# Revit family: Ladder_Ships_ALACO_Mezzanine-M60-80
name_source: partatom
category: Generic Models
units: mm (PartAtom-declared; Revit-internal decimal feet)

## family parameters
Can host rebar = No
Classification Number = 23.30.70.17.17
Cut with Voids When Loaded = No
Host = Face
Maintain Annotation Orientation = No
Part Type = Normal
Room Calculation Point = No
Round Connector Dimension = Use Diameter
Shared = No

## types (8) — shared parameters
Assembly Code = B1010700
Capacity = 1500 lbs per Rung
Default Elevation = 0' - 0"
Keynote = 05515
Manufacturer = ALACO Ladder Co
Manufacturer Fax = 909-591-7565
Manufacturer Website = http://alacoladder.com
Product Data = http://www.arcat.com
Revision = R1_2016-12
Standards Conformance = OSHA 1910.27
URL = http://alacoladder.com
Unit Width = 2' - 0"
handrailradius = 0' - 5 7/8"
zero-valued in all types: Expected Lifespan (Years), Maintenance Schedule (Months), Warranty Duration (Years)

## per-type parameters (varying)
| type | Description | Handrail Offset | Ladder Incline | Max Height | Model | Rail Depth | Step Height | Step Width | Top Step Offset from Surface | Use Extended Handrails | Use Flush Handrails |
| 80 Degree Incline Flush Handrail | ALACO Mezzanine Access Incline Ships Ladder - M80 as Specified | 0' - 7" | 80.00° | 14' - 0" | M80xxx | 0' - 2 13/16" | 0' - 11 13/16" | 0' - 3" | 0' - 2 1/4" | No | Yes |
| 75 Degree Incline Flush Handrail | ALACO Mezzanine Access Incline Ships Ladder - M75 as Specified | 0' - 7" | 75.00° | 17' - 0" | M75xxx | 0' - 4 1/8" | 0' - 11 5/8" | 0' - 4 1/4" | 0' - 1" | No | Yes |
| 70 Degree Incline Flush Handrail | ALACO Mezzanine Access Incline Ships Ladder - M70 as Specified | 0' - 7" | 70.00° | 17' - 0" | M70xxx | 0' - 4 1/8" | 0' - 11 1/4" | 0' - 4" | 0' - 0 7/8" | No | Yes |
| 60 Degree Incline Flush Handrail | ALACO Mezzanine Access Incline Ships Ladder - M60 as Specified | 1' - 0" | 60.00° | 15' - 0" | M60xxx | 0' - 5 3/8" | 0' - 10 7/16" | 0' - 5 15/16" | 0' - 0 3/4" | No | Yes |
| 80 Degree Incline Extended Handrail | ALACO Mezzanine Access Incline Ships Ladder - M80 as Specified | 0' - 7" | 80.00° | 14' - 0" | M80xxx | 0' - 2 13/16" | 0' - 11 13/16" | 0' - 3" | 0' - 2 1/4" | Yes | No |
| 75 Degree Incline Extended Handrail | ALACO Mezzanine Access Incline Ships Ladder - M75 as Specified | 0' - 7" | 75.00° | 17' - 0" | M75xxx | 0' - 4 1/8" | 0' - 11 5/8" | 0' - 4 1/4" | 0' - 1" | Yes | No |
| 70 Degree Incline Extended Handrail | ALACO Mezzanine Access Incline Ships Ladder - M70 as Specified | 0' - 7" | 70.00° | 17' - 0" | M70xxx | 0' - 4 1/8" | 0' - 11 1/4" | 0' - 4" | 0' - 0 7/8" | Yes | No |
| 60 Degree Incline Extended Handrail | ALACO Mezzanine Access Incline Ships Ladder - M60 as Specified | 1' - 0" | 60.00° | 15' - 0" | M60xxx | 0' - 5 3/8" | 0' - 10 7/16" | 0' - 5 15/16" | 0' - 0 3/4" | Yes | No |

## geometry (parser evidence)
native form markers: Sweep x4
no freeform markers — native parametric forms only
